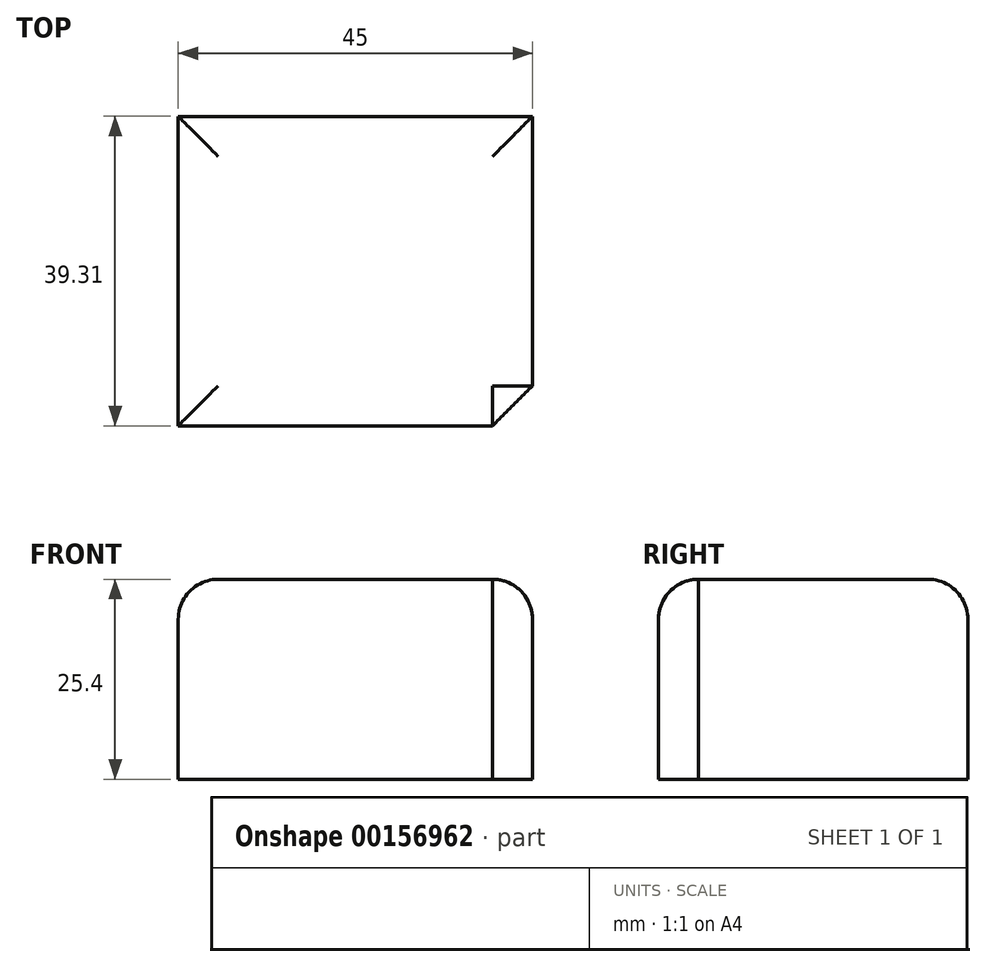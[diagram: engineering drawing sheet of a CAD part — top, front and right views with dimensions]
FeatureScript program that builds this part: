
annotation { "Feature Type Name" : "Feature", "Feature Type Description" : "" }
export const myFeature = defineFeature(function(context is Context, id is Id, definition is map)
    precondition{}
    {
        {
            var Q0;
            Q0=qCreatedBy(makeId("Top.planeOp"),FACE);
            var sketch = newSketch(context, id + "F0", { "sketchPlane" : qUnion([Q0])});
            skLineSegment(sketch, "E0.bottom", {"start": v(0, 0) * mm, "end": v(45, 0) * mm});
            skLineSegment(sketch, "E0.top", {"start": v(0, 39.3) * mm, "end": v(45, 39.3) * mm});
            skLineSegment(sketch, "E0.left", {"start": v(0, 0) * mm, "end": v(0, 39.3) * mm});
            skLineSegment(sketch, "E0.right", {"start": v(45, 0) * mm, "end": v(45, 39.3) * mm});
            skSolve(sketch);
        }
        {
            var Q0;
            Q0 = qSketchRegion(id + "F0", true);
            extrude(context, id + "F1", {"entities" : qUnion([Q0]), "depth" : 25.4 * mm});
        }
        {
            var Q0;
            Q0=makeQuery(id+"F1.opExtrude","CAP_FACE",FACE,{"disambiguationData":[OSD([sQuery(id+"F0.wireOp",EDGE,"E0.bottom"),sQuery(id+"F0.wireOp",EDGE,"E0.top"),sQuery(id+"F0.wireOp",EDGE,"E0.left"),sQuery(id+"F0.wireOp",EDGE,"E0.right")])],"isStart":false});
            fillet(context, id + "F2", {"entities" : qUnion([Q0]), "radius" : 5.08 * mm, "tangentPropagation" : true, "allowEdgeOverflow" : false});
        }
        {
            var Q0;
            Q0=makeQuery(id+"F1.opExtrude","SWEPT_EDGE",EDGE,{"disambiguationData":[OSD([sQuery(id+"F0.wireOp",EDGE,"E0.bottom"),sQuery(id+"F0.wireOp",EDGE,"E0.right")])]});
            chamfer(context, id + "F3", {"entities" : qUnion([Q0]), "width" : 5.08 * mm, "tangentPropagation" : true});
        }
    });
